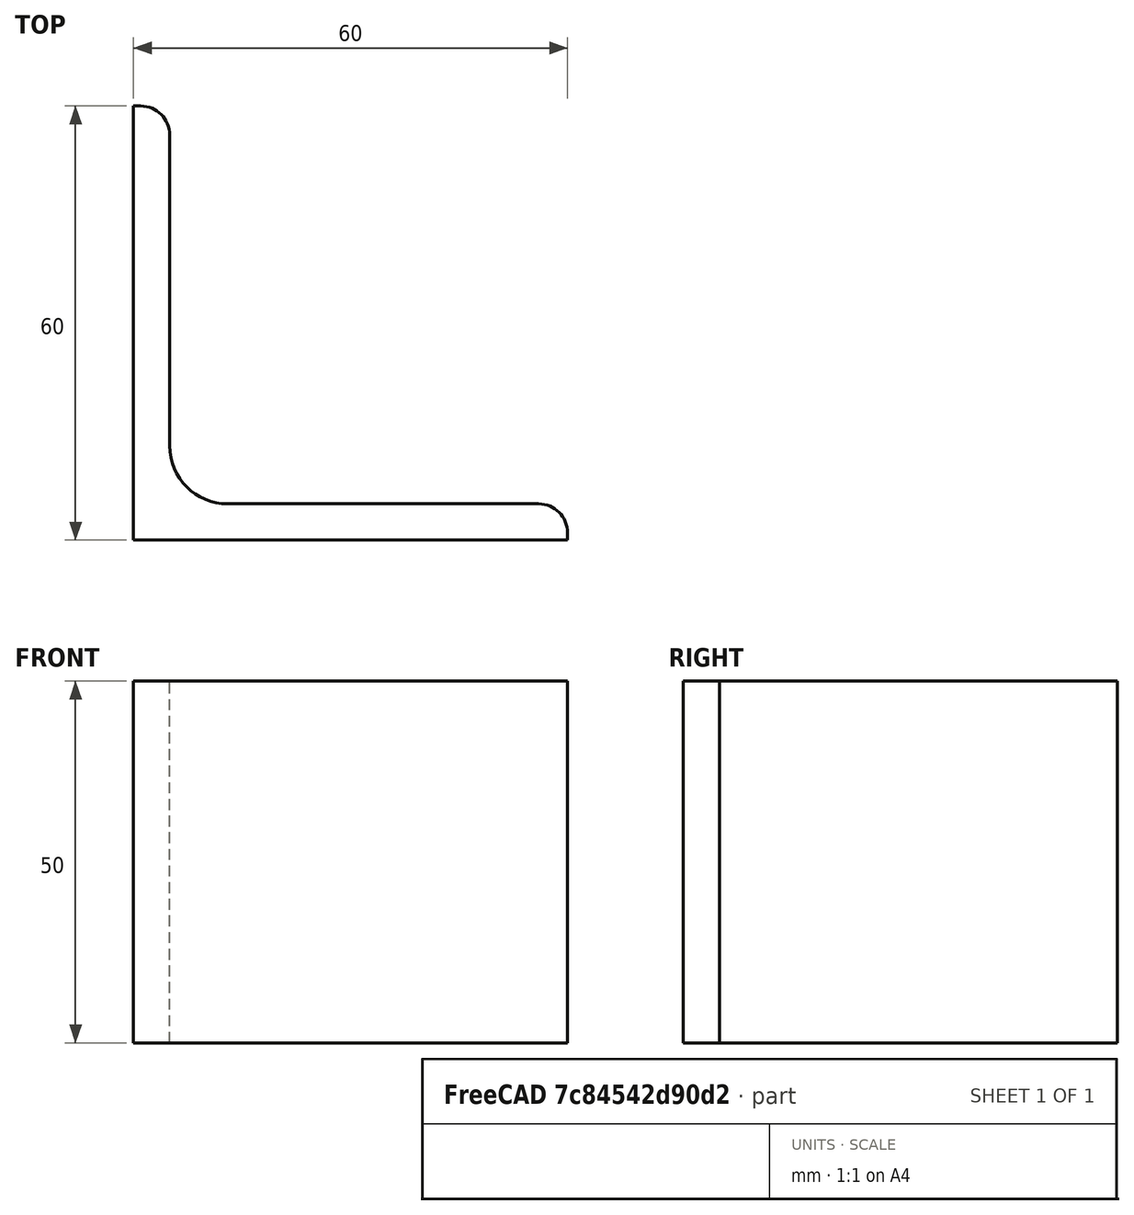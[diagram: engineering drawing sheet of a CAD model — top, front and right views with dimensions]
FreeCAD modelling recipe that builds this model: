
FCSTD DOCUMENT  (FreeCAD 0.15R4671 (Git))
Label: Angle Bar L60x60x5 EN10056 S235JR
License: All rights reserved
LicenseURL: http://en.wikipedia.org/wiki/All_rights_reserved
objects: Sketcher::SketchObject×1, Part::Extrusion×1
note: 2 computed .brp shape members not serialized (recipe doc carries the construction recipe); baked Part::Feature solids carry a one-line shape summary decoded from their .brp

FEATURE [Sketcher::SketchObject] Sketch
  sketch-geometry (9):
    g0: LineSegment StartX=0 StartY=0 StartZ=0 EndX=60 EndY=0 EndZ=0
    g1: LineSegment StartX=60 StartY=0 StartZ=0 EndX=60 EndY=1 EndZ=0
    g2: LineSegment StartX=56 StartY=5 StartZ=0 EndX=13 EndY=5 EndZ=0
    g3: LineSegment StartX=0 StartY=0 StartZ=0 EndX=0 EndY=60 EndZ=0
    g4: LineSegment StartX=0 StartY=60 StartZ=0 EndX=1 EndY=60 EndZ=0
    g5: LineSegment StartX=5 StartY=56 StartZ=0 EndX=5 EndY=13 EndZ=0
    g6: ArcOfCircle CenterX=13 CenterY=13 CenterZ=0 NormalX=0 NormalY=0 NormalZ=1 Radius=8 StartAngle=3.14159 EndAngle=4.71239
    g7: ArcOfCircle CenterX=1 CenterY=56 CenterZ=0 NormalX=0 NormalY=0 NormalZ=1 Radius=4 StartAngle=0 EndAngle=1.5708
    g8: ArcOfCircle CenterX=56 CenterY=1 CenterZ=0 NormalX=0 NormalY=0 NormalZ=1 Radius=4 StartAngle=0 EndAngle=1.5708
  constraints (23):
    c: Coincident(g0,g-1)
    c: Horizontal(g0)
    c: Coincident(g1,g0)
    c: Vertical(g1)
    c: Horizontal(g2)
    c: Coincident(g3,g-1)
    c: Vertical(g3)
    c: Coincident(g4,g3)
    c: Horizontal(g4)
    c: Vertical(g5)
    c: Tangent(g5,g6) = -1.5708
    c: Tangent(g2,g6) = 1.5708
    c: Tangent(g4,g7) = 1.5708
    c: Tangent(g5,g7) = 1.5708
    c: Tangent(g2,g8) = -1.5708
    c: Tangent(g1,g8) = -1.5708
    c: DistanceX(g0) = 60
    c: DistanceY(g3) = 60
    c: DistanceY(g0,g2) = 5
    c: DistanceX(g3,g5) = 5
    c: Radius(g6) = 8
    c: Radius(g8) = 4
    c: Radius(g7) = 4
FEATURE [Part::Extrusion] Extrude  label="Angle Bar L60x60x5 EN10056 S235JR"
  Base = -> Sketch
  Dir = (0,0,50)
  Solid = true
